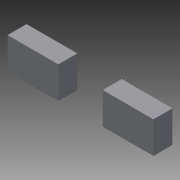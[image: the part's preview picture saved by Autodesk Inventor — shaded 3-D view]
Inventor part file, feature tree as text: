
AUTODESK INVENTOR PART (.ipt)
format: ipt  version: 2013 (Build 170138000, 138)  size: 86,528 bytes
history: native  units: in
note: dims shown in document units (in); Inventor stores cm internally (conversion verified against a paired STEP export)
features: extrude x2, sketch x2
ambient origin geometry x8: Origin, YZ Plane, XZ Plane, XY Plane, X Axis, Y Axis, Z Axis, Center Point
bodies: Solid1 (feature_tree)
feature tree (4):
  extrude  "Extrusion1"  Depth=4.0in
  extrude  "Extrusion2"  Depth=23.0in
  sketch  "Sketch1"  dims[d0=3.625in d1=4.0in]
  sketch  "Sketch2"  dims[d2=5.0in d3=23.0in d4=5.0in d5=3.0in d6=0.0in d7=8.0in d8=8.0in d9=3.0in d10=5.0in d11=0.0in]
